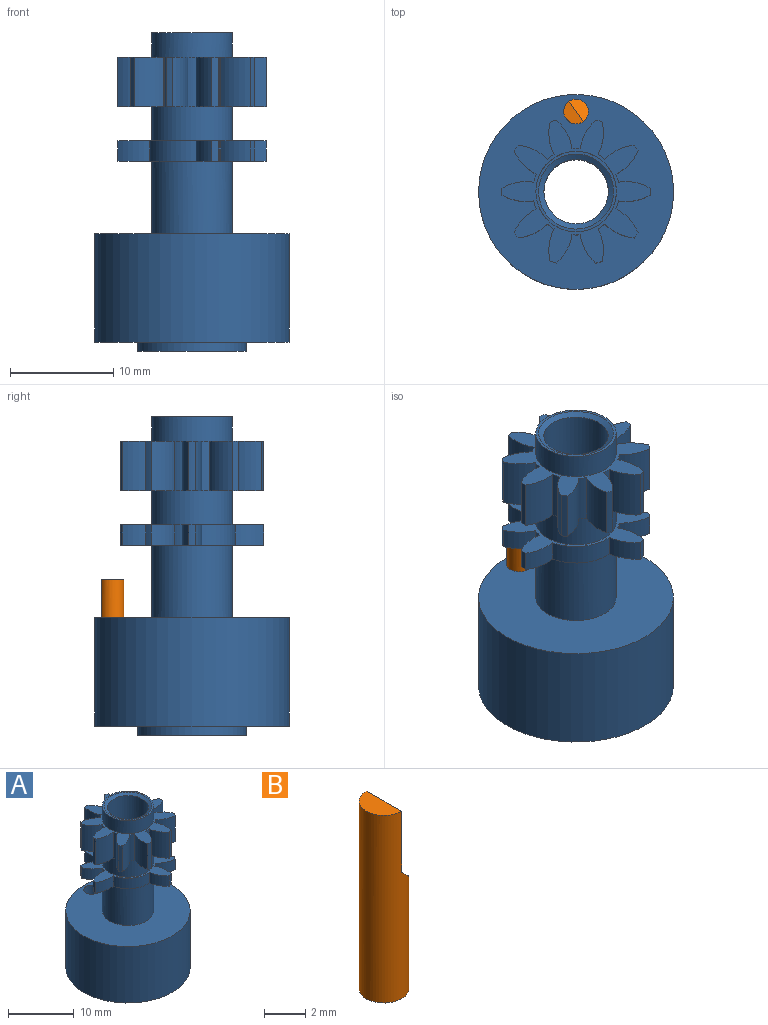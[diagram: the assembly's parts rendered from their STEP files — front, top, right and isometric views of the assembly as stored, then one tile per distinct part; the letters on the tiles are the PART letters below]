
ASSEMBLY  parts=2 mates=1
PART A: 89 faces, bbox 18.9x18.9x30.9 mm
  f0: cylinder r=3.9mm len=7.8mm, axis (0,0,-1), area 58.8mm2, adj f9,f87
  f1: cylinder r=3.9mm len=7.8mm, axis (0,0,-1), area 80.9mm2, adj f13,f88
  f2: cone r=3.12mm half-angle=30deg, axis (0,0,-1), area 49.7mm2, adj f3,f10
  f3: plane 10.5x10.5mm, normal (0,0,-1), area 31.2mm2, adj f2,f4
  f4: cylinder r=5.25mm len=10.5mm, axis (0,0,-1), area 29.7mm2, adj f3,f5
  f5: plane 18.9x18.9mm, normal (0,0,-1), area 189.4mm2, adj f4,f6,f11
  f6: cylinder r=9.45mm len=18.9mm, axis (0,0,-1), area 623.4mm2, adj f5,f7
  f7: plane 18.9x18.9mm, normal (0,0,1), area 228.2mm2, adj f6,f8,f11
  f8: cylinder r=3.9mm len=7.8mm, axis (0,0,-1), area 172.8mm2, adj f7,f14
  f9: plane 7.8x7.8mm, normal (0,0,1), area 6.2mm2, adj f0,f12
  f10: cylinder r=3.12mm len=28.73mm, axis (0,0,-1), area 563.2mm2, adj f2,f12
  f11: cylinder r=1.2mm len=10.5mm, axis (0,0,1), area 79.2mm2, adj f5,f7
  f12: cone r=3.64mm half-angle=60deg, axis (0,0,1), area 12.7mm2, adj f9,f10
  f13: plane 14.4x13.88mm, normal (0,0,1), area 46.7mm2, adj f1,f15,f16,f17,f18,f19,f20,f21
  f14: plane 14.4x13.88mm, normal (0,0,-1), area 46.7mm2, adj f8,f15,f16,f17,f18,f19,f20,f21
  f15: cylinder r=4.2mm len=1.95mm, axis (0,0,-1), area 1.6mm2, adj f13,f14,f16,f17
  f16: cylinder r=4.5mm len=2.3mm, axis (0,0,-1), area 6.3mm2, adj f13,f14,f15,f21
  f17: cylinder r=4.5mm len=3.09mm, axis (0,0,-1), area 6.3mm2, adj f13,f14,f15,f46
  f18: cylinder r=4.5mm len=2.85mm, axis (0,0,-1), area 6.3mm2, adj f13,f14,f19,f21
  f19: cylinder r=4.2mm len=1.95mm, axis (0,0,-1), area 1.6mm2, adj f13,f14,f18,f20
  f20: cylinder r=4.5mm len=3.12mm, axis (0,0,-1), area 6.3mm2, adj f13,f14,f19,f25
  f21: cylinder r=7.2mm len=1.95mm, axis (0,0,-1), area 1.2mm2, adj f13,f14,f16,f18
  f22: cylinder r=4.5mm len=2.76mm, axis (0,0,-1), area 6.3mm2, adj f13,f14,f23,f25
  f23: cylinder r=4.2mm len=1.95mm, axis (0,0,-1), area 1.6mm2, adj f13,f14,f22,f24
  f24: cylinder r=4.5mm len=2.76mm, axis (0,0,-1), area 6.3mm2, adj f13,f14,f23,f29
  f25: cylinder r=7.2mm len=1.95mm, axis (0,0,-1), area 1.2mm2, adj f13,f14,f20,f22
  f26: cylinder r=4.5mm len=3.12mm, axis (0,0,-1), area 6.3mm2, adj f13,f14,f27,f29
  f27: cylinder r=4.2mm len=1.95mm, axis (0,0,-1), area 1.6mm2, adj f13,f14,f26,f28
  f28: cylinder r=4.5mm len=2.85mm, axis (0,0,-1), area 6.3mm2, adj f13,f14,f27,f33
  f29: cylinder r=7.2mm len=1.95mm, axis (0,0,-1), area 1.2mm2, adj f13,f14,f24,f26
  f30: cylinder r=4.5mm len=2.3mm, axis (0,0,-1), area 6.3mm2, adj f13,f14,f31,f33
  f31: cylinder r=4.2mm len=1.95mm, axis (0,0,-1), area 1.6mm2, adj f13,f14,f30,f32
  f32: cylinder r=4.5mm len=3.09mm, axis (0,0,-1), area 6.3mm2, adj f13,f14,f31,f37
  f33: cylinder r=7.2mm len=1.95mm, axis (0,0,-1), area 1.2mm2, adj f13,f14,f28,f30
  f34: cylinder r=4.5mm len=3.09mm, axis (0,0,-1), area 6.3mm2, adj f13,f14,f35,f37
  f35: cylinder r=4.2mm len=1.95mm, axis (0,0,-1), area 1.6mm2, adj f13,f14,f34,f36
  f36: cylinder r=4.5mm len=2.3mm, axis (0,0,-1), area 6.3mm2, adj f13,f14,f35,f41
  f37: cylinder r=7.2mm len=1.95mm, axis (0,0,-1), area 1.2mm2, adj f13,f14,f32,f34
  f38: cylinder r=4.5mm len=2.85mm, axis (0,0,-1), area 6.3mm2, adj f13,f14,f39,f41
  f39: cylinder r=4.2mm len=1.95mm, axis (0,0,-1), area 1.6mm2, adj f13,f14,f38,f40
  f40: cylinder r=4.5mm len=3.12mm, axis (0,0,-1), area 6.3mm2, adj f13,f14,f39,f44
  f41: cylinder r=7.2mm len=1.95mm, axis (0,0,-1), area 1.2mm2, adj f13,f14,f36,f38
  f42: cylinder r=4.5mm len=2.76mm, axis (0,0,-1), area 6.3mm2, adj f13,f14,f43,f44
  f43: cylinder r=4.2mm len=4.5mm, axis (0,0,-1), area 11.9mm2, adj f13,f14,f42,f45
  f44: cylinder r=7.2mm len=1.95mm, axis (0,0,-1), area 1.2mm2, adj f13,f14,f40,f42
  f45: cylinder r=4.5mm len=3.09mm, axis (0,0,-1), area 6.3mm2, adj f13,f14,f43,f46
  f46: cylinder r=7.2mm len=1.95mm, axis (0,0,-1), area 1.2mm2, adj f13,f14,f17,f45
  f47: cylinder r=4.5mm len=4.8mm, axis (0,0,-1), area 15.4mm2, adj f48,f86,f87,f88
  f48: cylinder r=7.2mm len=4.8mm, axis (0,0,-1), area 3.1mm2, adj f47,f49,f87,f88
  f49: cylinder r=4.5mm len=4.8mm, axis (0,0,-1), area 15.4mm2, adj f48,f50,f87,f88
  f50: cylinder r=4.2mm len=4.8mm, axis (0,0,-1), area 3.9mm2, adj f49,f51,f87,f88
  f51: cylinder r=4.5mm len=4.8mm, axis (0,0,-1), area 15.4mm2, adj f50,f52,f87,f88
  f52: cylinder r=7.2mm len=4.8mm, axis (0,0,-1), area 3.1mm2, adj f51,f53,f87,f88
  f53: cylinder r=4.5mm len=4.8mm, axis (0,0,-1), area 15.4mm2, adj f52,f54,f87,f88
  f54: cylinder r=4.2mm len=4.8mm, axis (0,0,-1), area 3.9mm2, adj f53,f55,f87,f88
  f55: cylinder r=4.5mm len=4.8mm, axis (0,0,-1), area 15.4mm2, adj f54,f56,f87,f88
  f56: cylinder r=7.2mm len=4.8mm, axis (0,0,-1), area 3.1mm2, adj f55,f57,f87,f88
  f57: cylinder r=4.5mm len=4.8mm, axis (0,0,-1), area 15.4mm2, adj f56,f58,f87,f88
  f58: cylinder r=4.2mm len=4.8mm, axis (0,0,-1), area 3.9mm2, adj f57,f59,f87,f88
  f59: cylinder r=4.5mm len=4.8mm, axis (0,0,-1), area 15.4mm2, adj f58,f60,f87,f88
  f60: cylinder r=7.2mm len=4.8mm, axis (0,0,-1), area 3.1mm2, adj f59,f61,f87,f88
  f61: cylinder r=4.5mm len=4.8mm, axis (0,0,-1), area 15.4mm2, adj f60,f62,f87,f88
  f62: cylinder r=4.2mm len=4.8mm, axis (0,0,-1), area 3.9mm2, adj f61,f63,f87,f88
  f63: cylinder r=4.5mm len=4.8mm, axis (0,0,-1), area 15.4mm2, adj f62,f64,f87,f88
  f64: cylinder r=7.2mm len=4.8mm, axis (0,0,-1), area 3.1mm2, adj f63,f65,f87,f88
  f65: cylinder r=4.5mm len=4.8mm, axis (0,0,-1), area 15.4mm2, adj f64,f66,f87,f88
  f66: cylinder r=4.2mm len=4.8mm, axis (0,0,-1), area 3.9mm2, adj f65,f67,f87,f88
  f67: cylinder r=4.5mm len=4.8mm, axis (0,0,-1), area 15.4mm2, adj f66,f68,f87,f88
  f68: cylinder r=7.2mm len=4.8mm, axis (0,0,-1), area 3.1mm2, adj f67,f69,f87,f88
  f69: cylinder r=4.5mm len=4.8mm, axis (0,0,-1), area 15.4mm2, adj f68,f70,f87,f88
  f70: cylinder r=4.2mm len=4.8mm, axis (0,0,-1), area 3.9mm2, adj f69,f71,f87,f88
  f71: cylinder r=4.5mm len=4.8mm, axis (0,0,-1), area 15.4mm2, adj f70,f72,f87,f88
  f72: cylinder r=7.2mm len=4.8mm, axis (0,0,-1), area 3.1mm2, adj f71,f73,f87,f88
  f73: cylinder r=4.5mm len=4.8mm, axis (0,0,-1), area 15.4mm2, adj f72,f74,f87,f88
  f74: cylinder r=4.2mm len=4.8mm, axis (0,0,-1), area 3.9mm2, adj f73,f75,f87,f88
  f75: cylinder r=4.5mm len=4.8mm, axis (0,0,-1), area 15.4mm2, adj f74,f76,f87,f88
  f76: cylinder r=7.2mm len=4.8mm, axis (0,0,-1), area 3.1mm2, adj f75,f77,f87,f88
  f77: cylinder r=4.5mm len=4.8mm, axis (0,0,-1), area 15.4mm2, adj f76,f78,f87,f88
  f78: cylinder r=4.2mm len=4.8mm, axis (0,0,-1), area 3.9mm2, adj f77,f79,f87,f88
  f79: cylinder r=4.5mm len=4.8mm, axis (0,0,-1), area 15.4mm2, adj f78,f80,f87,f88
  f80: cylinder r=7.2mm len=4.8mm, axis (0,0,-1), area 3.1mm2, adj f79,f81,f87,f88
  f81: cylinder r=4.5mm len=4.8mm, axis (0,0,-1), area 15.4mm2, adj f80,f82,f87,f88
  f82: cylinder r=4.2mm len=4.8mm, axis (0,0,-1), area 3.9mm2, adj f81,f83,f87,f88
  f83: cylinder r=4.5mm len=4.8mm, axis (0,0,-1), area 15.4mm2, adj f82,f84,f87,f88
  f84: cylinder r=7.2mm len=4.8mm, axis (0,0,-1), area 3.1mm2, adj f83,f85,f87,f88
  f85: cylinder r=4.5mm len=4.8mm, axis (0,0,-1), area 15.4mm2, adj f84,f86,f87,f88
  f86: cylinder r=4.2mm len=4.8mm, axis (0,0,-1), area 3.9mm2, adj f47,f85,f87,f88
  f87: plane 14.4x13.88mm, normal (0,0,1), area 56.4mm2, adj f0,f47,f48,f49,f50,f51,f52,f53
  f88: plane 14.4x13.88mm, normal (0,0,-1), area 56.4mm2, adj f1,f47,f48,f49,f50,f51,f52,f53
PART B: 5 faces, bbox 2.4x2.4x11.1 mm
  f0: cylinder r=1.2mm len=11.1mm, axis (0,0,-1), area 67.2mm2, adj f1,f2,f3,f4
  f1: plane 2.4x1.2mm, normal (0,0,1), area 2.3mm2, adj f0,f3
  f2: plane 2.4x2.4mm, normal (0,0,-1), area 4.5mm2, adj f0
  f3: plane 3.6x2.4mm, normal (1,0,0), area 8.6mm2, adj f0,f1,f4
  f4: plane 2.4x1.2mm, normal (0.71,0,0.71), area 3.2mm2, adj f0,f3
PLACE A at identity fixed
PLACE B rot(axis=(0,0,1),36deg) t=(0,7.8,4)mm
MATE fastened B.f0 <-> A.f11  axis (0,0,-1) through (0,7.8,12.3)mm
